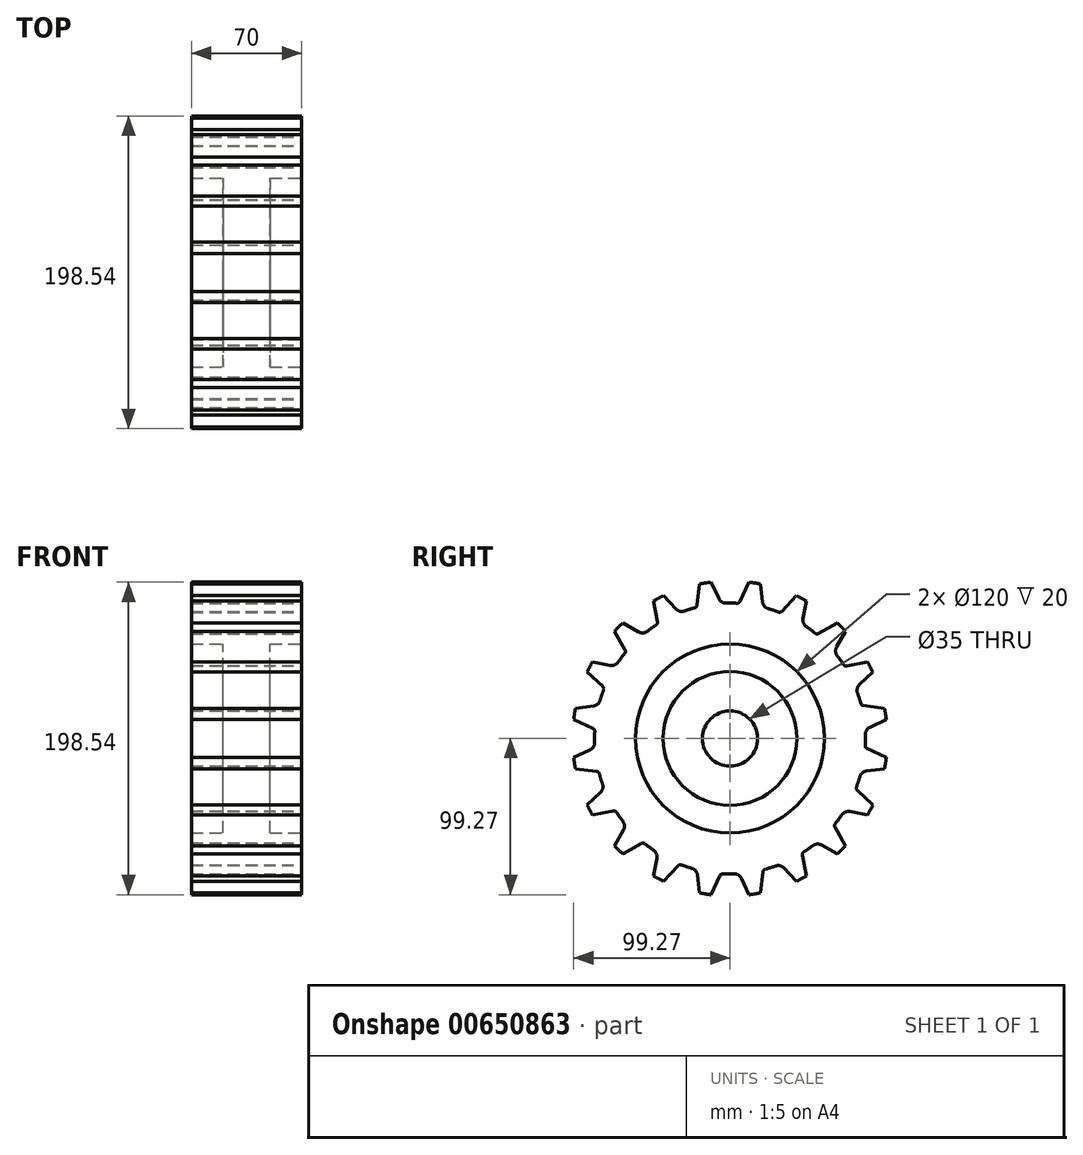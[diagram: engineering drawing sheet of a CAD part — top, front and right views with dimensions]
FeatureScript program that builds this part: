
annotation { "Feature Type Name" : "Feature", "Feature Type Description" : "" }
export const myFeature = defineFeature(function(context is Context, id is Id, definition is map)
    precondition{}
    {
        {
            var Q0;
            Q0=qCreatedBy(makeId("Front.planeOp"),FACE);
            var sketch = newSketch(context, id + "F0", { "sketchPlane" : qUnion([Q0])});
            skLineSegment(sketch, "E0.bottom", {"start": v(35, 20) * mm, "end": v(-35, 20) * mm});
            skLineSegment(sketch, "E0.top", {"start": v(35, -20) * mm, "end": v(15, -20) * mm});
            skLineSegment(sketch, "E0.left", {"start": v(35, 20) * mm, "end": v(35, -20) * mm});
            skLineSegment(sketch, "E0.right", {"start": v(-35, 20) * mm, "end": v(-35, -20) * mm});
            skPoint(sketch, "E0.middle", {"position": v(0, 0) * mm});
            skLineSegment(sketch, "E1.left", {"start": v(15, -37.5) * mm, "end": v(15, -20) * mm});
            skLineSegment(sketch, "E1.right", {"start": v(-15, -37.5) * mm, "end": v(-15, -20) * mm});
            skPoint(sketch, "E1.middle", {"position": v(0, -20) * mm});
            skLineSegment(sketch, "E2.bottom", {"start": v(35, -62.5) * mm, "end": v(-35, -62.5) * mm});
            skLineSegment(sketch, "E2.top", {"start": v(35, -37.5) * mm, "end": v(15, -37.5) * mm});
            skLineSegment(sketch, "E2.left", {"start": v(35, -62.5) * mm, "end": v(35, -37.5) * mm});
            skLineSegment(sketch, "E2.right", {"start": v(-35, -62.5) * mm, "end": v(-35, -37.5) * mm});
            skPoint(sketch, "E2.middle", {"position": v(0, -50) * mm});
            skPoint(sketch, "E1.top.start.orphan", {"position": v(15, 10) * mm});
            skPoint(sketch, "E3.orphan", {"position": v(-15, 10) * mm});
            skLineSegment(sketch, "E4.trimOffspring", {"start": v(-15, -37.5) * mm, "end": v(-35, -37.5) * mm});
            skPoint(sketch, "E1.bottom.end.orphan", {"position": v(-15, -50) * mm});
            skPoint(sketch, "E5.orphan", {"position": v(15, -50) * mm});
            skLineSegment(sketch, "E6.trimOffspring", {"start": v(-15, -20) * mm, "end": v(-35, -20) * mm});
            skLineSegment(sketch, "E7", {"start": v(0, 20) * mm, "end": v(0, -80) * mm, "construction": true});
            skLineSegment(sketch, "E8", {"start": v(0, -80) * mm, "end": v(-15, -80) * mm, "construction": true});
            skPoint(sketch, "E8.endSnap0", {"position": v(-15, -28.75) * mm});
            skSolve(sketch);
        }
        {
            var Q0;
            Q0=makeQuery(id+"F0.imprint","IMPRINT",FACE,{"disambiguationData":[TD([[makeQuery(id+"F0.imprint","IMPRINT",EDGE,{"derivedFrom":sQuery(id+"F0.wireOp",EDGE,"E0.bottom")}),1.0]])]});
            var Q1;
            Q1=sQuery(id+"F0.wireOp",EDGE,"E8");
            revolve(context, id + "F1", {"entities" : qUnion([Q0]), "axis" : qUnion([Q1]), "revolveType" : RevolveType.FULL});
        }
        {
            var Q0;
            Q0=makeQuery(id+"F1.opRevolve","SWEPT_FACE",FACE,{"disambiguationData":[OSD([sQuery(id+"F0.wireOp",EDGE,"E0.left")])]});
            var sketch = newSketch(context, id + "F2", { "sketchPlane" : qUnion([Q0])});
            skArc(sketch, "E9", {"start": v(4.4, 5.88) * mm, "mid": v(0.96, 5.99) * mm, "end": v(-2.49, 5.96) * mm});
            skLineSegment(sketch, "E10", {"start": v(0, -80) * mm, "end": v(0, 35.16) * mm, "construction": true});
            skLineSegment(sketch, "E11", {"start": v(6.32, 7.03) * mm, "end": v(12.03, 19.27) * mm});
            skLineSegment(sketch, "E12.MirrorCS", {"start": v(-7.16, 8.84) * mm, "end": v(-12.03, 19.27) * mm});
            skPoint(sketch, "E13.visualSharp", {"position": v(-5.75, 5.8) * mm});
            skArc(sketch, "E13.filletArc", {"start": v(-7.16, 8.84) * mm, "mid": v(-5.26, 6.7) * mm, "end": v(-2.49, 5.96) * mm});
            skPoint(sketch, "E14.visualSharp", {"position": v(5.75, 5.8) * mm});
            skArc(sketch, "E14.filletArc", {"start": v(4.4, 5.88) * mm, "mid": v(5.54, 6.16) * mm, "end": v(6.32, 7.03) * mm});
            skSolve(sketch);
        }
        {
            var Q0;
            Q0=makeQuery(id+"F2.imprint","IMPRINT",FACE,{"disambiguationData":[TD([[makeQuery(id+"F2.imprint","IMPRINT",EDGE,{"derivedFrom":sQuery(id+"F2.wireOp",EDGE,"E9")}),-1.0]])]});
            extrude(context, id + "F3", {"entities" : qUnion([Q0]), "operationType" : NewBodyOperationType.REMOVE, "endBound" : BoundingType.THROUGH_ALL, "oppositeDirection" : true, "depth" : 25 * mm, "offsetDistance" : 25 * mm});
        }
        {
            var Q0;
            Q0=makeQuery(id+"F3.boolean.opBoolean","COPY",FACE,{"derivedFrom":makeQuery(id+"F3.opExtrude","SWEPT_FACE",FACE,{"disambiguationData":[OSD([sQuery(id+"F2.wireOp",EDGE,"E12.MirrorCS")])]})});
            var Q1;
            Q1=makeQuery(id+"F3.boolean.opBoolean","COPY",FACE,{"derivedFrom":makeQuery(id+"F3.opExtrude","SWEPT_FACE",FACE,{"disambiguationData":[OSD([sQuery(id+"F2.wireOp",EDGE,"E13.filletArc")])]})});
            var Q2;
            Q2=makeQuery(id+"F3.boolean.opBoolean","COPY",FACE,{"derivedFrom":makeQuery(id+"F3.opExtrude","SWEPT_FACE",FACE,{"disambiguationData":[OSD([sQuery(id+"F2.wireOp",EDGE,"E9")])]})});
            var Q3;
            Q3=makeQuery(id+"F3.boolean.opBoolean","COPY",FACE,{"derivedFrom":makeQuery(id+"F3.opExtrude","SWEPT_FACE",FACE,{"disambiguationData":[OSD([sQuery(id+"F2.wireOp",EDGE,"E14.filletArc")])]})});
            var Q4;
            Q4=makeQuery(id+"F3.boolean.opBoolean","COPY",FACE,{"derivedFrom":makeQuery(id+"F3.opExtrude","SWEPT_FACE",FACE,{"disambiguationData":[OSD([sQuery(id+"F2.wireOp",EDGE,"E11")])]})});
            var Q5;
            Q5=makeQuery(id+"F1.opRevolve","SWEPT_FACE",FACE,{"disambiguationData":[OSD([sQuery(id+"F0.wireOp",EDGE,"E0.bottom")])]});
            circularPattern(context, id + "F4", {"patternType" : PatternType.FACE, "faces" : qUnion([Q0, Q1, Q2, Q3, Q4]), "axis" : qUnion([Q5]), "angle" : 9 * degree, "instanceCount" : 40});
        }
    });
